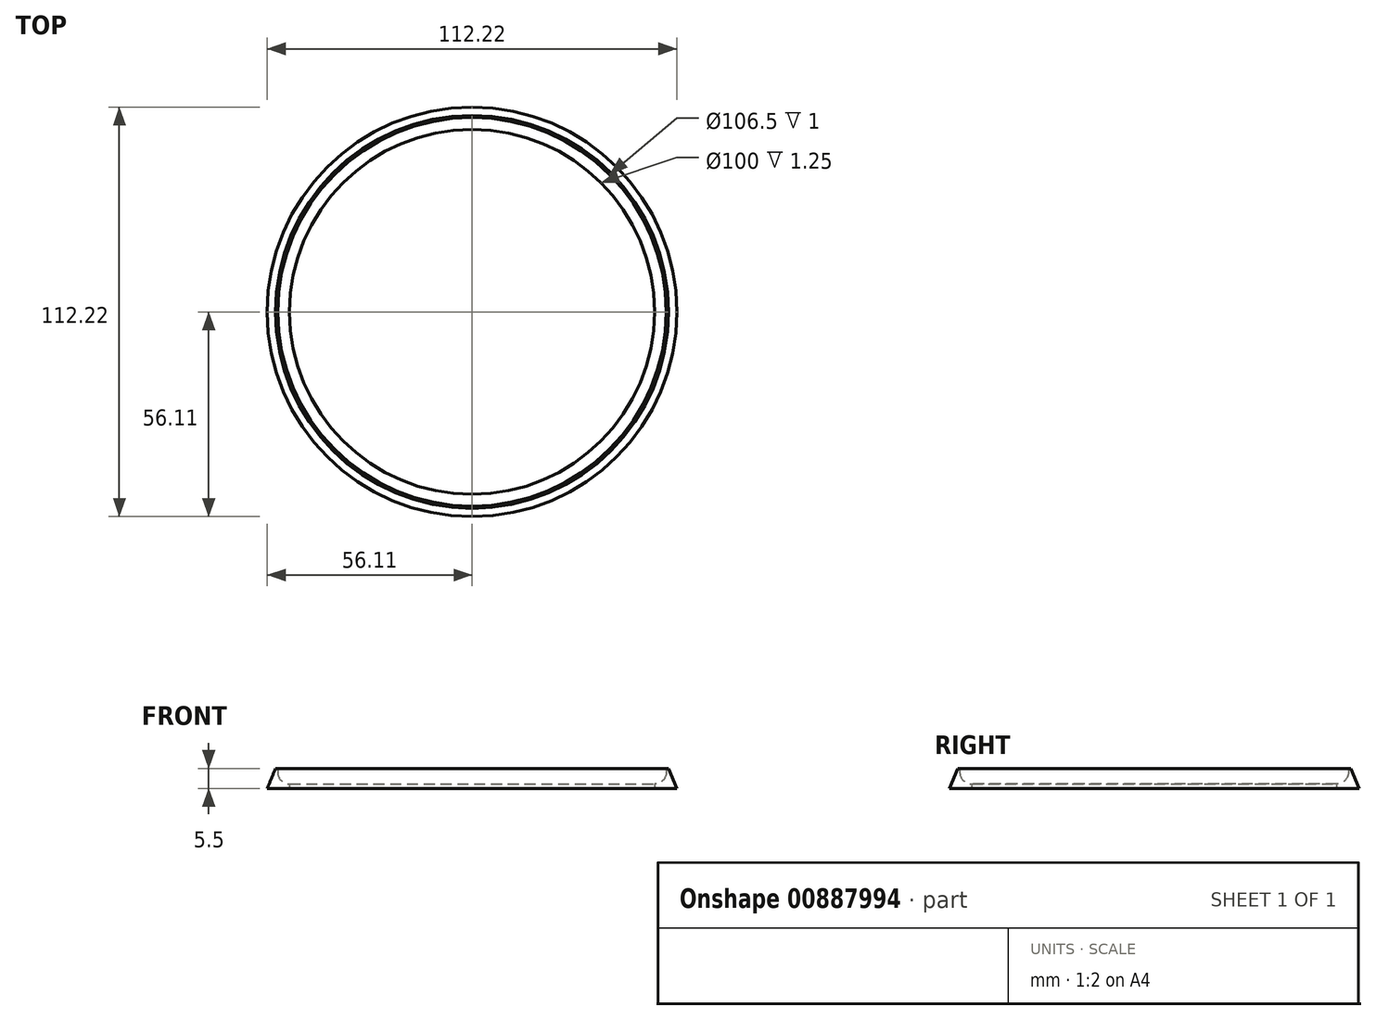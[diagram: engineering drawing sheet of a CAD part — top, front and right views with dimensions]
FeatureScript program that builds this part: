
annotation { "Feature Type Name" : "Feature", "Feature Type Description" : "" }
export const myFeature = defineFeature(function(context is Context, id is Id, definition is map)
    precondition{}
    {
        {
            var Q0;
            Q0=qCreatedBy(makeId("Front.planeOp"),FACE);
            var sketch = newSketch(context, id + "F0", { "sketchPlane" : qUnion([Q0])});
            skLineSegment(sketch, "E0", {"start": v(0, 0) * mm, "end": v(-50, 0) * mm});
            skLineSegment(sketch, "E1", {"start": v(-50, 0) * mm, "end": v(-53.25, 0) * mm});
            skCircle(sketch, "E2", {"center": v(-50, 0) * mm, "radius": 3.25 * mm});
            skLineSegment(sketch, "E3", {"start": v(-46.75, 0) * mm, "end": v(-45.75, 0) * mm});
            skLineSegment(sketch, "E4", {"start": v(-53.25, 0) * mm, "end": v(-54.25, 0) * mm});
            skLineSegment(sketch, "E5", {"start": v(-54.25, 0) * mm, "end": v(-56.11, -4.5) * mm});
            skLineSegment(sketch, "E6", {"start": v(-56.11, -4.5) * mm, "end": v(-43.89, -4.5) * mm});
            skLineSegment(sketch, "E7", {"start": v(-43.89, -4.5) * mm, "end": v(-45.75, 0) * mm});
            skLineSegment(sketch, "E8", {"start": v(-50, 0) * mm, "end": v(-50, -4.5) * mm});
            skLineSegment(sketch, "E9", {"start": v(0, 0.65) * mm, "end": v(0, 9.25) * mm});
            skLineSegment(sketch, "E10", {"start": v(-54.25, 0) * mm, "end": v(-54.25, 1) * mm});
            skLineSegment(sketch, "E11", {"start": v(-54.25, 1) * mm, "end": v(-53.25, 1) * mm});
            skLineSegment(sketch, "E12", {"start": v(-53.25, 1) * mm, "end": v(-53.25, 0) * mm});
            skLineSegment(sketch, "E13", {"start": v(-45.75, 0) * mm, "end": v(-45.75, 1) * mm});
            skLineSegment(sketch, "E14", {"start": v(-45.75, 1) * mm, "end": v(-46.75, 1) * mm});
            skLineSegment(sketch, "E15", {"start": v(-46.75, 1) * mm, "end": v(-46.75, 0) * mm});
            skLineSegment(sketch, "E16", {"start": v(-54.25, 0) * mm, "end": v(-53.84, 1) * mm});
            skLineSegment(sketch, "E17", {"start": v(-45.75, 0) * mm, "end": v(-46.16, 1) * mm});
            skSolve(sketch);
        }
        {
            var Q0;
            {var subQ1=sQuery(id+"F0.wireOp",EDGE,"E4");Q0=makeQuery(id+"F0.imprint","IMPRINT",FACE,{"disambiguationData":[TD([[makeQuery(id+"F0.imprint","IMPRINT",EDGE,{"derivedFrom":subQ1}),1.0]])]});}
            var Q1;
            {var subQ1=sQuery(id+"F0.wireOp",EDGE,"E3");Q1=makeQuery(id+"F0.imprint","IMPRINT",FACE,{"disambiguationData":[TD([[makeQuery(id+"F0.imprint","IMPRINT",EDGE,{"derivedFrom":subQ1}),-1.0]])]});}
            var Q2;
            Q2=makeQuery(id+"F0.imprint","IMPRINT",FACE,{"disambiguationData":[TD([[makeQuery(id+"F0.imprint","IMPRINT",EDGE,{"derivedFrom":sQuery(id+"F0.wireOp",EDGE,"E4")}),-1.0]])]});
            var Q3;
            Q3=makeQuery(id+"F0.imprint","IMPRINT",FACE,{"disambiguationData":[TD([[makeQuery(id+"F0.imprint","IMPRINT",EDGE,{"derivedFrom":sQuery(id+"F0.wireOp",EDGE,"E3")}),1.0]])]});
            var Q4;
            Q4=sQuery(id+"F0.wireOp",EDGE,"E9");
            revolve(context, id + "F1", {"surfaceOperationType" : NewSurfaceOperationType.NEW, "entities" : qUnion([Q0, Q1, Q2, Q3]), "axis" : qUnion([Q4]), "revolveType" : RevolveType.FULL});
        }
    });
